# Revit family: IMH_ARR_1,9
name_source: partatom
category: Mechanical Equipment
units: mm (PartAtom-declared; Revit-internal decimal feet)

## family parameters
Always vertical = No
Cut with Voids When Loaded = No
Part Type = Normal
Room Calculation Point = No
Round Connector Dimension = Use Radius
Shared = No
Work Plane-Based = No

## types (44) — shared parameters
1.5 = 1.5 "
90 = 90.00°
BAD = No
BAD_CCW = No
BAD_CW = No
BAU = No
BAU_CCW = No
BAU_CW = No
BHD = No
BHD_CCW = No
BHD_CW = No
CCW = No
CW = Yes
DBD = No
DBD_CCW = No
DBD_CW = No
Four = 4 "
L_RAD = 18.156 "
Manufacturer = Loren Cook Company
NO = No
ONE EIGTH = 0.125 "
One_Inch = 1 "
TAD = No
TAD_CCW = No
TAD_CW = No
TAU = No
TAU_CCW = No
TAU_CW = No
THD = Yes
THD_CCW = No
THD_CW = Yes
Three = 3 "
Two_Feet = 24 "
Two_Inches = 2 "
UBD = No
UBD_CCW = No
UBD_CW = No
URL = www.lorencook.com
ZERO = 0.00°
zero-valued in all types: 0, FIRST_CURVE

## per-type parameters (varying)
- 70_MHA_ARR_1_9: 2S=8.5 "; 2T=2.375 "; 91_AA=8.019 "; A=6.625 "; A+.25=6.875 "; A/2=3.313 "; A/5=1.325 "; AA=8.813 "; B=5.875 "; B3=6.125 "; B4=-3.063 "; B5=3.063 "; BB=8.375 "; C=7 "; C3=3.375 "; C4=5.5 "; D=14.25 "; D3=-14.125 "; DimQ=7.438 "; E=9.688 "; E_LESS_2=7.688 "; F=21.063 "; G=26.25 "; H=24.188 "; HALF_B=2.938 "; HALF_C=3.5 "; HALF_E=4.844 "; HALF_M=4.156 "; HALF_P=0.281 "; HALF_T=0.594 "; J=4 "; K=9.188 "; L=9.688 "; M=8.313 "; M3=6.988 "; M4=6.988 "; Model=MHA; N=10.563 "; NA=3.938 "; NA3=1.969 "; NEG_D=-14.25 "; NEG_F=-21.063 "; P=0.563 "; R=14.875 "; R3=-11.156 "; R4=-11.156 "; S=4.25 "; SECOND_CURVE=0.828 "; T=1.188 "; T3=3.375 "; THIRD_CURVE=1.104 "; Type Comments=Industrial Material Handler Backward Inclined Flat Blade Belt Driven Single Width Single Inlet Arrangement 1_9; U=6.188 "; UNIT_SIZE=70; W=6 "; X=10.125 "; Y=9.25 "; Z=13.375 "
- 90_MHA_ARR_1_9: 2S=10.125 "; 2T=2.875 "; 91_AA=10.181 "; A=8.438 "; A+.25=8.688 "; A/2=4.219 "; A/5=1.688 "; AA=11.188 "; B=7.5 "; B3=7.75 "; B4=-3.875 "; B5=3.875 "; BB=10.625 "; C=9 "; C3=4.375 "; C4=6.5 "; D=15.25 "; D3=-15.125 "; DimQ=7.438 "; E=9.688 "; E_LESS_2=7.688 "; F=21.875 "; G=27.875 "; H=28.75 "; HALF_B=3.75 "; HALF_C=4.5 "; HALF_E=4.844 "; HALF_M=5.313 "; HALF_P=0.281 "; HALF_T=0.719 "; J=4 "; K=9.188 "; L=12.313 "; M=10.625 "; M3=8.938 "; M4=8.938 "; Model=MHA; N=13.5 "; NA=5.063 "; NA3=2.531 "; NEG_D=-15.25 "; NEG_F=-21.875 "; P=0.563 "; R=14.875 "; R3=-11.156 "; R4=-11.156 "; S=5.063 "; SECOND_CURVE=1.055 "; T=1.438 "; T3=3.875 "; THIRD_CURVE=1.406 "; Type Comments=Industrial Material Handler Backward Inclined Flat Blade Belt Driven Single Width Single Inlet Arrangement 1_9; U=7 "; UNIT_SIZE=90; W=6 "; X=12.938 "; Y=11.75 "; Z=17.063 "
- 110_MHA_ARR_1_9: 2S=13 "; 2T=2.875 "; 91_AA=12.513 "; A=10.375 "; A+.25=10.625 "; A/2=5.188 "; A/5=2.075 "; AA=13.75 "; B=9.125 "; B3=9.375 "; B4=-4.688 "; B5=4.688 "; BB=13.063 "; C=11 "; C3=5.375 "; C4=7.5 "; D=18.75 "; D3=-18.625 "; DimQ=8.25 "; E=9.688 "; E_LESS_2=7.688 "; F=25 "; G=32.875 "; H=35.188 "; HALF_B=4.563 "; HALF_C=5.5 "; HALF_E=4.844 "; HALF_M=6.5 "; HALF_P=0.281 "; HALF_T=0.719 "; J=4 "; K=9.188 "; L=15.063 "; M=13 "; M3=10.925 "; M4=10.925 "; Model=MHA; N=16.438 "; NA=6.063 "; NA3=3.031 "; NEG_D=-18.75 "; NEG_F=-25 "; P=0.563 "; R=16.5 "; R3=-12.375 "; R4=-12.375 "; S=6.5 "; SECOND_CURVE=1.297 "; T=1.438 "; T3=3.875 "; THIRD_CURVE=1.729 "; Type Comments=Industrial Material Handler Backward Inclined Flat Blade Belt Driven Single Width Single Inlet Arrangement 1_9; U=8.813 "; UNIT_SIZE=110; W=8 "; X=15.75 "; Y=14.438 "; Z=20.813 "
- 130_MHA_ARR_1_9: 2S=14.75 "; 2T=3.375 "; 91_AA=14.731 "; A=12.188 "; A+.25=12.438 "; A/2=6.094 "; A/5=2.438 "; AA=16.188 "; B=10.875 "; B3=11.125 "; B4=-5.563 "; B5=5.563 "; BB=15.375 "; C=13 "; C3=6.375 "; C4=8.5 "; D=21.75 "; D3=-21.625 "; DimQ=8.375 "; E=11.75 "; E_LESS_2=9.75 "; F=26.188 "; G=34.875 "; H=41.188 "; HALF_B=5.438 "; HALF_C=6.5 "; HALF_E=5.875 "; HALF_M=7.688 "; HALF_P=0.344 "; HALF_T=0.844 "; J=5 "; K=11 "; L=17.813 "; M=15.375 "; M3=12.938 "; M4=12.938 "; Model=MHA; N=19.438 "; NA=7.25 "; NA3=3.625 "; NEG_D=-21.75 "; NEG_F=-26.188 "; P=0.688 "; R=16.75 "; R3=-12.563 "; R4=-12.563 "; S=7.375 "; SECOND_CURVE=1.523 "; T=1.688 "; T3=4.375 "; THIRD_CURVE=2.031 "; Type Comments=Industrial Material Handler Backward Inclined Flat Blade Belt Driven Single Width Single Inlet Arrangement 1_9; U=9.813 "; UNIT_SIZE=130; W=8 "; X=18.625 "; Y=17 "; Z=24.625 "
- 150_MHA_ARR_1_9: 2S=16.438 "; 2T=3.875 "; 91_AA=17.176 "; A=14.063 "; A+.25=14.313 "; A/2=7.031 "; A/5=2.813 "; AA=18.875 "; B=12.563 "; B3=12.813 "; B4=-6.406 "; B5=6.406 "; BB=18 "; C=15 "; C3=7.375 "; C4=9.5 "; D=25.25 "; D3=-25.125 "; DimQ=10.75 "; E=13 "; E_LESS_2=11 "; F=31.75 "; G=41.313 "; H=47.625 "; HALF_B=6.281 "; HALF_C=7.5 "; HALF_E=6.5 "; HALF_M=8.875 "; HALF_P=0.344 "; HALF_T=0.969 "; J=5 "; K=12.25 "; L=20.625 "; M=17.75 "; M3=14.938 "; M4=14.938 "; Model=MHA; N=22.375 "; NA=8.313 "; NA3=4.156 "; NEG_D=-25.25 "; NEG_F=-31.75 "; P=0.688 "; R=21.5 "; R3=-16.125 "; R4=-16.125 "; S=8.219 "; SECOND_CURVE=1.758 "; T=1.938 "; T3=4.875 "; THIRD_CURVE=2.344 "; Type Comments=Industrial Material Handler Backward Inclined Flat Blade Belt Driven Single Width Single Inlet Arrangement 1_9; U=10.688 "; UNIT_SIZE=150; W=8 "; X=21.5 "; Y=19.75 "; Z=28.375 "
- 170_MHA_ARR_1_9: 2S=18.125 "; 2T=4.375 "; 91_AA=19.338 "; A=16 "; A+.25=16.25 "; A/2=8 "; A/5=3.2 "; AA=21.25 "; B=14.25 "; B3=14.5 "; B4=-7.25 "; B5=7.25 "; BB=20.25 "; C=17 "; C3=8.375 "; C4=10.5 "; D=28.25 "; D3=-28.125 "; DimQ=10.75 "; E=13.875 "; E_LESS_2=11.875 "; F=32.563 "; G=43 "; H=53.625 "; HALF_B=7.125 "; HALF_C=8.5 "; HALF_E=6.938 "; HALF_M=10.063 "; HALF_P=0.344 "; HALF_T=1.094 "; J=6 "; K=13.125 "; L=23.75 "; M=20.125 "; M3=16.925 "; M4=16.925 "; Model=MHA; N=25.375 "; NA=9.375 "; NA3=4.688 "; NEG_D=-28.25 "; NEG_F=-32.563 "; P=0.688 "; R=21.5 "; R3=-16.125 "; R4=-16.125 "; S=9.063 "; SECOND_CURVE=2 "; T=2.188 "; T3=5.375 "; THIRD_CURVE=2.667 "; Type Comments=Industrial Material Handler Backward Inclined Flat Blade Belt Driven Single Width Single Inlet Arrangement 1_9; U=11.5 "; UNIT_SIZE=170; W=8 "; X=24.563 "; Y=22.5 "; Z=32.188 "
- 190_MHA_ARR_1_9: 2S=19.875 "; 2T=4.875 "; 91_AA=21.613 "; A=17.813 "; A+.25=18.063 "; A/2=8.906 "; A/5=3.563 "; AA=23.75 "; B=15.875 "; B3=16.125 "; B4=-8.063 "; B5=8.063 "; BB=22.625 "; C=19 "; C3=9.375 "; C4=11.5 "; D=31.25 "; D3=-31.125 "; DimQ=11.375 "; E=15.313 "; E_LESS_2=13.313 "; F=34.688 "; G=46 "; H=59.5 "; HALF_B=7.938 "; HALF_C=9.5 "; HALF_E=7.656 "; HALF_M=11.219 "; HALF_P=0.344 "; HALF_T=1.219 "; J=6 "; K=14.563 "; L=25.938 "; M=22.438 "; M3=18.875 "; M4=18.875 "; Model=MHA; N=28.25 "; NA=10.438 "; NA3=5.219 "; NEG_D=-31.25 "; NEG_F=-34.688 "; P=0.688 "; R=22.75 "; R3=-17.063 "; R4=-17.063 "; S=9.938 "; SECOND_CURVE=2.227 "; T=2.438 "; T3=5.875 "; THIRD_CURVE=2.969 "; Type Comments=Industrial Material Handler Backward Inclined Flat Blade Belt Driven Single Width Single Inlet Arrangement 1_9; U=12.313 "; UNIT_SIZE=190; W=8 "; X=27.125 "; Y=24.875 "; Z=35.813 "
- 210_MHA_ARR_1_9: 2S=21.313 "; 2T=4.875 "; 91_AA=23.433 "; A=19.75 "; A+.25=20 "; A/2=9.875 "; A/5=3.95 "; AA=25.75 "; B=17.563 "; B3=17.813 "; B4=-8.906 "; B5=8.906 "; BB=24.375 "; C=21 "; C3=10.375 "; C4=12.5 "; D=34.5 "; D3=-34.375 "; DimQ=12.75 "; E=16.563 "; E_LESS_2=14.563 "; F=38.25 "; G=50.375 "; H=65.75 "; HALF_B=8.781 "; HALF_C=10.5 "; HALF_E=8.281 "; HALF_M=11.5 "; HALF_P=0.344 "; HALF_T=1.219 "; J=6 "; K=15.813 "; L=28.5 "; M=23 "; M3=19.05 "; M4=19.05 "; Model=MHA; N=31.25 "; NA=11.5 "; NA3=5.75 "; NEG_D=-34.5 "; NEG_F=-38.25 "; P=0.688 "; R=25.5 "; R3=-19.125 "; R4=-19.125 "; S=10.656 "; SECOND_CURVE=2.469 "; T=2.438 "; T3=5.875 "; THIRD_CURVE=3.292 "; Type Comments=Industrial Material Handler Backward Inclined Flat Blade Belt Driven Single Width Single Inlet Arrangement 1_9; U=13.188 "; UNIT_SIZE=210; W=8 "; X=29.875 "; Y=27.125 "; Z=38.375 "
- 230_MHA_ARR_1_9: 2S=24.625 "; 2T=5.375 "; 91_AA=25.764 "; A=21.625 "; A+.25=21.875 "; A/2=10.813 "; A/5=4.325 "; AA=28.313 "; B=19.25 "; B3=19.5 "; B4=-9.75 "; B5=9.75 "; BB=26.813 "; C=23 "; C3=11.375 "; C4=13.5 "; D=37.5 "; D3=-37.375 "; DimQ=13.438 "; E=18.813 "; E_LESS_2=16.813 "; F=41.125 "; G=55.25 "; H=71.813 "; HALF_B=9.625 "; HALF_C=11.5 "; HALF_E=9.406 "; HALF_M=13 "; HALF_P=0.406 "; HALF_T=1.344 "; J=7 "; K=17.563 "; L=31.25 "; M=26 "; M3=21.675 "; M4=21.675 "; Model=MHA; N=34.313 "; NA=12.688 "; NA3=6.344 "; NEG_D=-37.5 "; NEG_F=-41.125 "; P=0.813 "; R=26.875 "; R3=-20.156 "; R4=-20.156 "; S=12.313 "; SECOND_CURVE=2.703 "; T=2.688 "; T3=6.375 "; THIRD_CURVE=3.604 "; Type Comments=Industrial Material Handler Backward Inclined Flat Blade Belt Driven Single Width Single Inlet Arrangement 1_9; U=15.125 "; UNIT_SIZE=230; W=8 "; X=32.813 "; Y=29.813 "; Z=42.625 "
- 260_MHA_ARR_1_9: 2S=27.125 "; 2T=5.375 "; 91_AA=29.006 "; A=24.438 "; A+.25=24.688 "; A/2=12.219 "; A/5=4.888 "; AA=31.875 "; B=21.75 "; B3=22 "; B4=-11 "; B5=11 "; BB=30.25 "; C=26 "; C3=12.875 "; C4=15 "; D=41.75 "; D3=-41.625 "; DimQ=13.875 "; E=20.625 "; E_LESS_2=18.625 "; F=43.938 "; G=58.688 "; H=82.938 "; HALF_B=10.875 "; HALF_C=13 "; HALF_E=10.313 "; HALF_M=14.5 "; HALF_P=0.406 "; HALF_T=1.344 "; J=7 "; K=19.375 "; L=35.125 "; M=29 "; M3=24.113 "; M4=24.113 "; Model=MHA; N=41.188 "; NA=16.75 "; NA3=8.375 "; NEG_D=-41.75 "; NEG_F=-43.938 "; P=0.813 "; R=27.75 "; R3=-20.813 "; R4=-20.813 "; S=13.563 "; SECOND_CURVE=3.055 "; T=2.688 "; T3=6.375 "; THIRD_CURVE=4.073 "; Type Comments=Industrial Material Handler Backward Inclined Flat Blade Belt Driven Single Width Single Inlet Arrangement 1_9; U=16.375 "; UNIT_SIZE=260; W=8 "; X=38.188 "; Y=33.5 "; Z=49.625 "
- 290_MHA_ARR_1_9: 2S=29.625 "; 2T=5.875 "; 91_AA=32.533 "; A=27.313 "; A+.25=27.563 "; A/2=13.656 "; A/5=5.463 "; AA=35.75 "; B=24.25 "; B3=24.5 "; B4=-12.25 "; B5=12.25 "; BB=33.875 "; C=29 "; C3=14.375 "; C4=16.5 "; D=46.5 "; D3=-46.375 "; DimQ=14.375 "; E=22.5 "; E_LESS_2=20.5 "; F=45.563 "; G=62.188 "; H=92.5 "; HALF_B=12.125 "; HALF_C=14.5 "; HALF_E=11.25 "; HALF_M=15.875 "; HALF_P=0.406 "; HALF_T=1.469 "; J=8 "; K=21.25 "; L=39.5 "; M=31.75 "; M3=26.288 "; M4=26.288 "; Model=MHA; N=45.875 "; NA=18.563 "; NA3=9.281 "; NEG_D=-46.5 "; NEG_F=-45.563 "; P=0.813 "; R=28.75 "; R3=-21.563 "; R4=-21.563 "; S=14.813 "; SECOND_CURVE=3.414 "; T=2.938 "; T3=6.875 "; THIRD_CURVE=4.552 "; Type Comments=Industrial Material Handler Backward Inclined Flat Blade Belt Driven Single Width Single Inlet Arrangement 1_9; U=17.625 "; UNIT_SIZE=290; W=8 "; X=42.688 "; Y=37.625 "; Z=54.875 "
- 110_MHB_ARR_1_9: 2S=13 "; 2T=2.875 "; 91_AA=12.513 "; A=10.375 "; A+.25=10.625 "; A/2=5.188 "; A/5=2.075 "; AA=13.75 "; B=9.125 "; B3=9.375 "; B4=-4.688 "; B5=4.688 "; BB=13.063 "; C=11 "; C3=5.375 "; C4=7.5 "; D=18.75 "; D3=-18.625 "; DimQ=8.25 "; E=9.688 "; E_LESS_2=7.688 "; F=25 "; G=32.875 "; H=35.188 "; HALF_B=4.563 "; HALF_C=5.5 "; HALF_E=4.844 "; HALF_M=6.5 "; HALF_P=0.281 "; HALF_T=0.719 "; J=4 "; K=9.188 "; L=15.063 "; M=13 "; M3=10.925 "; M4=10.925 "; Model=MHB; N=16.438 "; NA=6.063 "; NA3=3.031 "; NEG_D=-18.75 "; NEG_F=-25 "; P=0.563 "; R=16.5 "; R3=-12.375 "; R4=-12.375 "; S=6.5 "; SECOND_CURVE=1.297 "; T=1.438 "; T3=3.875 "; THIRD_CURVE=1.729 "; Type Comments=Industrial Material Handler Backward Inclined Backplated Radial Blade Belt Driven Single Width Single Inlet Arrangement 1_9; U=8.813 "; UNIT_SIZE=110; W=8 "; X=15.75 "; Y=14.438 "; Z=20.813 "
- 110_MHR_ARR_1_9: 2S=13 "; 2T=2.875 "; 91_AA=12.513 "; A=10.375 "; A+.25=10.625 "; A/2=5.188 "; A/5=2.075 "; AA=13.75 "; B=9.125 "; B3=9.375 "; B4=-4.688 "; B5=4.688 "; BB=13.063 "; C=11 "; C3=5.375 "; C4=7.5 "; D=18.75 "; D3=-18.625 "; DimQ=8.25 "; E=9.688 "; E_LESS_2=7.688 "; F=25 "; G=32.875 "; H=35.188 "; HALF_B=4.563 "; HALF_C=5.5 "; HALF_E=4.844 "; HALF_M=6.5 "; HALF_P=0.281 "; HALF_T=0.719 "; J=4 "; K=9.188 "; L=15.063 "; M=13 "; M3=10.925 "; M4=10.925 "; Model=MHR; N=16.438 "; NA=6.063 "; NA3=3.031 "; NEG_D=-18.75 "; NEG_F=-25 "; P=0.563 "; R=16.5 "; R3=-12.375 "; R4=-12.375 "; S=6.5 "; SECOND_CURVE=1.297 "; T=1.438 "; T3=3.875 "; THIRD_CURVE=1.729 "; Type Comments=Industrial Material Handler Backward Inclined Reinforced Radial Blade Belt Driven Single Width Single Inlet Arrangement 1_9; U=8.813 "; UNIT_SIZE=110; W=8 "; X=15.75 "; Y=14.438 "; Z=20.813 "
- 130_MHB_ARR_1_9: 2S=14.75 "; 2T=3.375 "; 91_AA=14.731 "; A=12.188 "; A+.25=12.438 "; A/2=6.094 "; A/5=2.438 "; AA=16.188 "; B=10.875 "; B3=11.125 "; B4=-5.563 "; B5=5.563 "; BB=15.375 "; C=13 "; C3=6.375 "; C4=8.5 "; D=21.75 "; D3=-21.625 "; DimQ=8.375 "; E=11.75 "; E_LESS_2=9.75 "; F=26.188 "; G=34.875 "; H=41.188 "; HALF_B=5.438 "; HALF_C=6.5 "; HALF_E=5.875 "; HALF_M=7.688 "; HALF_P=0.344 "; HALF_T=0.844 "; J=5 "; K=11 "; L=17.813 "; M=15.375 "; M3=12.938 "; M4=12.938 "; Model=MHB; N=19.438 "; NA=7.25 "; NA3=3.625 "; NEG_D=-21.75 "; NEG_F=-26.188 "; P=0.688 "; R=16.75 "; R3=-12.563 "; R4=-12.563 "; S=7.375 "; SECOND_CURVE=1.523 "; T=1.688 "; T3=4.375 "; THIRD_CURVE=2.031 "; Type Comments=Industrial Material Handler Backward Inclined Backplated Radial Blade Belt Driven Single Width Single Inlet Arrangement 1_9; U=9.813 "; UNIT_SIZE=130; W=8 "; X=18.625 "; Y=17 "; Z=24.625 "
- 130_MHR_ARR_1_9: 2S=14.75 "; 2T=3.375 "; 91_AA=14.731 "; A=12.188 "; A+.25=12.438 "; A/2=6.094 "; A/5=2.438 "; AA=16.188 "; B=10.875 "; B3=11.125 "; B4=-5.563 "; B5=5.563 "; BB=15.375 "; C=13 "; C3=6.375 "; C4=8.5 "; D=21.75 "; D3=-21.625 "; DimQ=8.375 "; E=11.75 "; E_LESS_2=9.75 "; F=26.188 "; G=34.875 "; H=41.188 "; HALF_B=5.438 "; HALF_C=6.5 "; HALF_E=5.875 "; HALF_M=7.688 "; HALF_P=0.344 "; HALF_T=0.844 "; J=5 "; K=11 "; L=17.813 "; M=15.375 "; M3=12.938 "; M4=12.938 "; Model=MHR; N=19.438 "; NA=7.25 "; NA3=3.625 "; NEG_D=-21.75 "; NEG_F=-26.188 "; P=0.688 "; R=16.75 "; R3=-12.563 "; R4=-12.563 "; S=7.375 "; SECOND_CURVE=1.523 "; T=1.688 "; T3=4.375 "; THIRD_CURVE=2.031 "; Type Comments=Industrial Material Handler Backward Inclined Reinforced Radial Blade Belt Driven Single Width Single Inlet Arrangement 1_9; U=9.813 "; UNIT_SIZE=130; W=8 "; X=18.625 "; Y=17 "; Z=24.625 "
- 150_MHB_ARR_1_9: 2S=16.438 "; 2T=3.875 "; 91_AA=17.176 "; A=14.063 "; A+.25=14.313 "; A/2=7.031 "; A/5=2.813 "; AA=18.875 "; B=12.563 "; B3=12.813 "; B4=-6.406 "; B5=6.406 "; BB=18 "; C=15 "; C3=7.375 "; C4=9.5 "; D=25.25 "; D3=-25.125 "; DimQ=10.75 "; E=13 "; E_LESS_2=11 "; F=31.75 "; G=41.313 "; H=47.625 "; HALF_B=6.281 "; HALF_C=7.5 "; HALF_E=6.5 "; HALF_M=8.875 "; HALF_P=0.344 "; HALF_T=0.969 "; J=5 "; K=12.25 "; L=20.625 "; M=17.75 "; M3=14.938 "; M4=14.938 "; Model=MHB; N=22.375 "; NA=8.313 "; NA3=4.156 "; NEG_D=-25.25 "; NEG_F=-31.75 "; P=0.688 "; R=21.5 "; R3=-16.125 "; R4=-16.125 "; S=8.219 "; SECOND_CURVE=1.758 "; T=1.938 "; T3=4.875 "; THIRD_CURVE=2.344 "; Type Comments=Industrial Material Handler Backward Inclined Backplated Radial Blade Belt Driven Single Width Single Inlet Arrangement 1_9; U=10.688 "; UNIT_SIZE=150; W=8 "; X=21.5 "; Y=19.75 "; Z=28.375 "
- 150_MHR_ARR_1_9: 2S=16.438 "; 2T=3.875 "; 91_AA=17.176 "; A=14.063 "; A+.25=14.313 "; A/2=7.031 "; A/5=2.813 "; AA=18.875 "; B=12.563 "; B3=12.813 "; B4=-6.406 "; B5=6.406 "; BB=18 "; C=15 "; C3=7.375 "; C4=9.5 "; D=25.25 "; D3=-25.125 "; DimQ=10.75 "; E=13 "; E_LESS_2=11 "; F=31.75 "; G=41.313 "; H=47.625 "; HALF_B=6.281 "; HALF_C=7.5 "; HALF_E=6.5 "; HALF_M=8.875 "; HALF_P=0.344 "; HALF_T=0.969 "; J=5 "; K=12.25 "; L=20.625 "; M=17.75 "; M3=14.938 "; M4=14.938 "; Model=MHR; N=22.375 "; NA=8.313 "; NA3=4.156 "; NEG_D=-25.25 "; NEG_F=-31.75 "; P=0.688 "; R=21.5 "; R3=-16.125 "; R4=-16.125 "; S=8.219 "; SECOND_CURVE=1.758 "; T=1.938 "; T3=4.875 "; THIRD_CURVE=2.344 "; Type Comments=Industrial Material Handler Backward Inclined Reinforced Radial Blade Belt Driven Single Width Single Inlet Arrangement 1_9; U=10.688 "; UNIT_SIZE=150; W=8 "; X=21.5 "; Y=19.75 "; Z=28.375 "
- 170_MHB_ARR_1_9: 2S=18.125 "; 2T=4.375 "; 91_AA=19.338 "; A=16 "; A+.25=16.25 "; A/2=8 "; A/5=3.2 "; AA=21.25 "; B=14.25 "; B3=14.5 "; B4=-7.25 "; B5=7.25 "; BB=20.25 "; C=17 "; C3=8.375 "; C4=10.5 "; D=28.25 "; D3=-28.125 "; DimQ=10.75 "; E=13.875 "; E_LESS_2=11.875 "; F=32.563 "; G=43 "; H=53.625 "; HALF_B=7.125 "; HALF_C=8.5 "; HALF_E=6.938 "; HALF_M=10.063 "; HALF_P=0.344 "; HALF_T=1.094 "; J=6 "; K=13.125 "; L=23.75 "; M=20.125 "; M3=16.925 "; M4=16.925 "; Model=MHB; N=25.375 "; NA=9.375 "; NA3=4.688 "; NEG_D=-28.25 "; NEG_F=-32.563 "; P=0.688 "; R=21.5 "; R3=-16.125 "; R4=-16.125 "; S=9.063 "; SECOND_CURVE=2 "; T=2.188 "; T3=5.375 "; THIRD_CURVE=2.667 "; Type Comments=Industrial Material Handler Backward Inclined Backplated Radial Blade Belt Driven Single Width Single Inlet Arrangement 1_9; U=11.5 "; UNIT_SIZE=170; W=8 "; X=24.563 "; Y=22.5 "; Z=32.188 "
- 170_MHR_ARR_1_9: 2S=18.125 "; 2T=4.375 "; 91_AA=19.338 "; A=16 "; A+.25=16.25 "; A/2=8 "; A/5=3.2 "; AA=21.25 "; B=14.25 "; B3=14.5 "; B4=-7.25 "; B5=7.25 "; BB=20.25 "; C=17 "; C3=8.375 "; C4=10.5 "; D=28.25 "; D3=-28.125 "; DimQ=10.75 "; E=13.875 "; E_LESS_2=11.875 "; F=32.563 "; G=43 "; H=53.625 "; HALF_B=7.125 "; HALF_C=8.5 "; HALF_E=6.938 "; HALF_M=10.063 "; HALF_P=0.344 "; HALF_T=1.094 "; J=6 "; K=13.125 "; L=23.75 "; M=20.125 "; M3=16.925 "; M4=16.925 "; Model=MHR; N=25.375 "; NA=9.375 "; NA3=4.688 "; NEG_D=-28.25 "; NEG_F=-32.563 "; P=0.688 "; R=21.5 "; R3=-16.125 "; R4=-16.125 "; S=9.063 "; SECOND_CURVE=2 "; T=2.188 "; T3=5.375 "; THIRD_CURVE=2.667 "; Type Comments=Industrial Material Handler Backward Inclined Reinforced Radial Blade Belt Driven Single Width Single Inlet Arrangement 1_9; U=11.5 "; UNIT_SIZE=170; W=8 "; X=24.563 "; Y=22.5 "; Z=32.188 "
- 190_MHB_ARR_1_9: 2S=19.875 "; 2T=4.875 "; 91_AA=21.613 "; A=17.813 "; A+.25=18.063 "; A/2=8.906 "; A/5=3.563 "; AA=23.75 "; B=15.875 "; B3=16.125 "; B4=-8.063 "; B5=8.063 "; BB=22.625 "; C=19 "; C3=9.375 "; C4=11.5 "; D=31.25 "; D3=-31.125 "; DimQ=11.375 "; E=15.313 "; E_LESS_2=13.313 "; F=34.688 "; G=46 "; H=59.5 "; HALF_B=7.938 "; HALF_C=9.5 "; HALF_E=7.656 "; HALF_M=11.219 "; HALF_P=0.344 "; HALF_T=1.219 "; J=6 "; K=14.563 "; L=25.938 "; M=22.438 "; M3=18.875 "; M4=18.875 "; Model=MHB; N=28.25 "; NA=10.438 "; NA3=5.219 "; NEG_D=-31.25 "; NEG_F=-34.688 "; P=0.688 "; R=22.75 "; R3=-17.063 "; R4=-17.063 "; S=9.938 "; SECOND_CURVE=2.227 "; T=2.438 "; T3=5.875 "; THIRD_CURVE=2.969 "; Type Comments=Industrial Material Handler Backward Inclined Backplated Radial Blade Belt Driven Single Width Single Inlet Arrangement 1_9; U=12.313 "; UNIT_SIZE=190; W=8 "; X=27.125 "; Y=24.875 "; Z=35.813 "
- 190_MHR_ARR_1_9: 2S=19.875 "; 2T=4.875 "; 91_AA=21.613 "; A=17.813 "; A+.25=18.063 "; A/2=8.906 "; A/5=3.563 "; AA=23.75 "; B=15.875 "; B3=16.125 "; B4=-8.063 "; B5=8.063 "; BB=22.625 "; C=19 "; C3=9.375 "; C4=11.5 "; D=31.25 "; D3=-31.125 "; DimQ=11.375 "; E=15.313 "; E_LESS_2=13.313 "; F=34.688 "; G=46 "; H=59.5 "; HALF_B=7.938 "; HALF_C=9.5 "; HALF_E=7.656 "; HALF_M=11.219 "; HALF_P=0.344 "; HALF_T=1.219 "; J=6 "; K=14.563 "; L=25.938 "; M=22.438 "; M3=18.875 "; M4=18.875 "; Model=MHR; N=28.25 "; NA=10.438 "; NA3=5.219 "; NEG_D=-31.25 "; NEG_F=-34.688 "; P=0.688 "; R=22.75 "; R3=-17.063 "; R4=-17.063 "; S=9.938 "; SECOND_CURVE=2.227 "; T=2.438 "; T3=5.875 "; THIRD_CURVE=2.969 "; Type Comments=Industrial Material Handler Backward Inclined Reinforced Radial Blade Belt Driven Single Width Single Inlet Arrangement 1_9; U=12.313 "; UNIT_SIZE=190; W=8 "; X=27.125 "; Y=24.875 "; Z=35.813 "
- 210_MHB_ARR_1_9: 2S=21.313 "; 2T=4.875 "; 91_AA=23.433 "; A=19.75 "; A+.25=20 "; A/2=9.875 "; A/5=3.95 "; AA=25.75 "; B=17.563 "; B3=17.813 "; B4=-8.906 "; B5=8.906 "; BB=24.375 "; C=21 "; C3=10.375 "; C4=12.5 "; D=34.5 "; D3=-34.375 "; DimQ=12.75 "; E=16.563 "; E_LESS_2=14.563 "; F=38.25 "; G=50.375 "; H=65.75 "; HALF_B=8.781 "; HALF_C=10.5 "; HALF_E=8.281 "; HALF_M=11.5 "; HALF_P=0.344 "; HALF_T=1.219 "; J=6 "; K=15.813 "; L=28.5 "; M=23 "; M3=19.05 "; M4=19.05 "; Model=MHB; N=31.25 "; NA=11.5 "; NA3=5.75 "; NEG_D=-34.5 "; NEG_F=-38.25 "; P=0.688 "; R=25.5 "; R3=-19.125 "; R4=-19.125 "; S=10.656 "; SECOND_CURVE=2.469 "; T=2.438 "; T3=5.875 "; THIRD_CURVE=3.292 "; Type Comments=Industrial Material Handler Backward Inclined Backplated Radial Blade Belt Driven Single Width Single Inlet Arrangement 1_9; U=13.188 "; UNIT_SIZE=210; W=8 "; X=29.875 "; Y=27.125 "; Z=38.375 "
- 210_MHR_ARR_1_9: 2S=21.313 "; 2T=4.875 "; 91_AA=23.433 "; A=19.75 "; A+.25=20 "; A/2=9.875 "; A/5=3.95 "; AA=25.75 "; B=17.563 "; B3=17.813 "; B4=-8.906 "; B5=8.906 "; BB=24.375 "; C=21 "; C3=10.375 "; C4=12.5 "; D=34.5 "; D3=-34.375 "; DimQ=12.75 "; E=16.563 "; E_LESS_2=14.563 "; F=38.25 "; G=50.375 "; H=65.75 "; HALF_B=8.781 "; HALF_C=10.5 "; HALF_E=8.281 "; HALF_M=11.5 "; HALF_P=0.344 "; HALF_T=1.219 "; J=6 "; K=15.813 "; L=28.5 "; M=23 "; M3=19.05 "; M4=19.05 "; Model=MHR; N=31.25 "; NA=11.5 "; NA3=5.75 "; NEG_D=-34.5 "; NEG_F=-38.25 "; P=0.688 "; R=25.5 "; R3=-19.125 "; R4=-19.125 "; S=10.656 "; SECOND_CURVE=2.469 "; T=2.438 "; T3=5.875 "; THIRD_CURVE=3.292 "; Type Comments=Industrial Material Handler Backward Inclined Reinforced Radial Blade Belt Driven Single Width Single Inlet Arrangement 1_9; U=13.188 "; UNIT_SIZE=210; W=8 "; X=29.875 "; Y=27.125 "; Z=38.375 "
- 230_MHB_ARR_1_9: 2S=24.625 "; 2T=5.375 "; 91_AA=25.764 "; A=21.625 "; A+.25=21.875 "; A/2=10.813 "; A/5=4.325 "; AA=28.313 "; B=19.25 "; B3=19.5 "; B4=-9.75 "; B5=9.75 "; BB=26.813 "; C=23 "; C3=11.375 "; C4=13.5 "; D=37.5 "; D3=-37.375 "; DimQ=13.438 "; E=18.813 "; E_LESS_2=16.813 "; F=41.125 "; G=55.25 "; H=71.813 "; HALF_B=9.625 "; HALF_C=11.5 "; HALF_E=9.406 "; HALF_M=13 "; HALF_P=0.406 "; HALF_T=1.344 "; J=7 "; K=17.563 "; L=31.25 "; M=26 "; M3=21.675 "; M4=21.675 "; Model=MHB; N=34.313 "; NA=12.688 "; NA3=6.344 "; NEG_D=-37.5 "; NEG_F=-41.125 "; P=0.813 "; R=26.875 "; R3=-20.156 "; R4=-20.156 "; S=12.313 "; SECOND_CURVE=2.703 "; T=2.688 "; T3=6.375 "; THIRD_CURVE=3.604 "; Type Comments=Industrial Material Handler Backward Inclined Backplated Radial Blade Belt Driven Single Width Single Inlet Arrangement 1_9; U=15.125 "; UNIT_SIZE=230; W=8 "; X=32.813 "; Y=29.813 "; Z=42.625 "
- 230_MHR_ARR_1_9: 2S=24.625 "; 2T=5.375 "; 91_AA=25.764 "; A=21.625 "; A+.25=21.875 "; A/2=10.813 "; A/5=4.325 "; AA=28.313 "; B=19.25 "; B3=19.5 "; B4=-9.75 "; B5=9.75 "; BB=26.813 "; C=23 "; C3=11.375 "; C4=13.5 "; D=37.5 "; D3=-37.375 "; DimQ=13.438 "; E=18.813 "; E_LESS_2=16.813 "; F=41.125 "; G=55.25 "; H=71.813 "; HALF_B=9.625 "; HALF_C=11.5 "; HALF_E=9.406 "; HALF_M=13 "; HALF_P=0.406 "; HALF_T=1.344 "; J=7 "; K=17.563 "; L=31.25 "; M=26 "; M3=21.675 "; M4=21.675 "; Model=MHR; N=34.313 "; NA=12.688 "; NA3=6.344 "; NEG_D=-37.5 "; NEG_F=-41.125 "; P=0.813 "; R=26.875 "; R3=-20.156 "; R4=-20.156 "; S=12.313 "; SECOND_CURVE=2.703 "; T=2.688 "; T3=6.375 "; THIRD_CURVE=3.604 "; Type Comments=Industrial Material Handler Backward Inclined Reinforced Radial Blade Belt Driven Single Width Single Inlet Arrangement 1_9; U=15.125 "; UNIT_SIZE=230; W=8 "; X=32.813 "; Y=29.813 "; Z=42.625 "
- 260_MHB_ARR_1_9: 2S=27.125 "; 2T=5.375 "; 91_AA=29.006 "; A=24.438 "; A+.25=24.688 "; A/2=12.219 "; A/5=4.888 "; AA=31.875 "; B=21.75 "; B3=22 "; B4=-11 "; B5=11 "; BB=30.25 "; C=26 "; C3=12.875 "; C4=15 "; D=41.75 "; D3=-41.625 "; DimQ=13.875 "; E=20.625 "; E_LESS_2=18.625 "; F=43.938 "; G=58.688 "; H=82.938 "; HALF_B=10.875 "; HALF_C=13 "; HALF_E=10.313 "; HALF_M=14.5 "; HALF_P=0.406 "; HALF_T=1.344 "; J=7 "; K=19.375 "; L=35.125 "; M=29 "; M3=24.113 "; M4=24.113 "; Model=MHB; N=41.188 "; NA=16.75 "; NA3=8.375 "; NEG_D=-41.75 "; NEG_F=-43.938 "; P=0.813 "; R=27.75 "; R3=-20.813 "; R4=-20.813 "; S=13.563 "; SECOND_CURVE=3.055 "; T=2.688 "; T3=6.375 "; THIRD_CURVE=4.073 "; Type Comments=Industrial Material Handler Backward Inclined Backplated Radial Blade Belt Driven Single Width Single Inlet Arrangement 1_9; U=16.375 "; UNIT_SIZE=260; W=8 "; X=38.188 "; Y=33.5 "; Z=49.625 "
- 260_MHR_ARR_1_9: 2S=27.125 "; 2T=5.375 "; 91_AA=29.006 "; A=24.438 "; A+.25=24.688 "; A/2=12.219 "; A/5=4.888 "; AA=31.875 "; B=21.75 "; B3=22 "; B4=-11 "; B5=11 "; BB=30.25 "; C=26 "; C3=12.875 "; C4=15 "; D=41.75 "; D3=-41.625 "; DimQ=13.875 "; E=20.625 "; E_LESS_2=18.625 "; F=43.938 "; G=58.688 "; H=82.938 "; HALF_B=10.875 "; HALF_C=13 "; HALF_E=10.313 "; HALF_M=14.5 "; HALF_P=0.406 "; HALF_T=1.344 "; J=7 "; K=19.375 "; L=35.125 "; M=29 "; M3=24.113 "; M4=24.113 "; Model=MHR; N=41.188 "; NA=16.75 "; NA3=8.375 "; NEG_D=-41.75 "; NEG_F=-43.938 "; P=0.813 "; R=27.75 "; R3=-20.813 "; R4=-20.813 "; S=13.563 "; SECOND_CURVE=3.055 "; T=2.688 "; T3=6.375 "; THIRD_CURVE=4.073 "; Type Comments=Industrial Material Handler Backward Inclined Reinforced Radial Blade Belt Driven Single Width Single Inlet Arrangement 1_9; U=16.375 "; UNIT_SIZE=260; W=8 "; X=38.188 "; Y=33.5 "; Z=49.625 "
- 290_MHB_ARR_1_9: 2S=29.625 "; 2T=5.875 "; 91_AA=32.533 "; A=27.313 "; A+.25=27.563 "; A/2=13.656 "; A/5=5.463 "; AA=35.75 "; B=24.25 "; B3=24.5 "; B4=-12.25 "; B5=12.25 "; BB=33.875 "; C=29 "; C3=14.375 "; C4=16.5 "; D=46.5 "; D3=-46.375 "; DimQ=14.375 "; E=22.5 "; E_LESS_2=20.5 "; F=45.563 "; G=62.188 "; H=92.5 "; HALF_B=12.125 "; HALF_C=14.5 "; HALF_E=11.25 "; HALF_M=15.875 "; HALF_P=0.406 "; HALF_T=1.469 "; J=8 "; K=21.25 "; L=39.5 "; M=31.75 "; M3=26.288 "; M4=26.288 "; Model=MHB; N=45.875 "; NA=18.563 "; NA3=9.281 "; NEG_D=-46.5 "; NEG_F=-45.563 "; P=0.813 "; R=28.75 "; R3=-21.563 "; R4=-21.563 "; S=14.813 "; SECOND_CURVE=3.414 "; T=2.938 "; T3=6.875 "; THIRD_CURVE=4.552 "; Type Comments=Industrial Material Handler Backward Inclined Backplated Radial Blade Belt Driven Single Width Single Inlet Arrangement 1_9; U=17.625 "; UNIT_SIZE=290; W=8 "; X=42.688 "; Y=37.625 "; Z=54.875 "
- 290_MHR_ARR_1_9: 2S=29.625 "; 2T=5.875 "; 91_AA=32.533 "; A=27.313 "; A+.25=27.563 "; A/2=13.656 "; A/5=5.463 "; AA=35.75 "; B=24.25 "; B3=24.5 "; B4=-12.25 "; B5=12.25 "; BB=33.875 "; C=29 "; C3=14.375 "; C4=16.5 "; D=46.5 "; D3=-46.375 "; DimQ=14.375 "; E=22.5 "; E_LESS_2=20.5 "; F=45.563 "; G=62.188 "; H=92.5 "; HALF_B=12.125 "; HALF_C=14.5 "; HALF_E=11.25 "; HALF_M=15.875 "; HALF_P=0.406 "; HALF_T=1.469 "; J=8 "; K=21.25 "; L=39.5 "; M=31.75 "; M3=26.288 "; M4=26.288 "; Model=MHR; N=45.875 "; NA=18.563 "; NA3=9.281 "; NEG_D=-46.5 "; NEG_F=-45.563 "; P=0.813 "; R=28.75 "; R3=-21.563 "; R4=-21.563 "; S=14.813 "; SECOND_CURVE=3.414 "; T=2.938 "; T3=6.875 "; THIRD_CURVE=4.552 "; Type Comments=Industrial Material Handler Backward Inclined Reinforced Radial Blade Belt Driven Single Width Single Inlet Arrangement 1_9; U=17.625 "; UNIT_SIZE=290; W=8 "; X=42.688 "; Y=37.625 "; Z=54.875 "
- 70_MHB_ARR_1_9: 2S=8.5 "; 2T=2.375 "; 91_AA=8.019 "; A=6.625 "; A+.25=6.875 "; A/2=3.313 "; A/5=1.325 "; AA=8.813 "; B=5.875 "; B3=6.125 "; B4=-3.063 "; B5=3.063 "; BB=8.375 "; C=7 "; C3=3.375 "; C4=5.5 "; D=14.25 "; D3=-14.125 "; DimQ=7.438 "; E=9.688 "; E_LESS_2=7.688 "; F=21.063 "; G=26.25 "; H=24.188 "; HALF_B=2.938 "; HALF_C=3.5 "; HALF_E=4.844 "; HALF_M=4.156 "; HALF_P=0.281 "; HALF_T=0.594 "; J=4 "; K=9.188 "; L=9.688 "; M=8.313 "; M3=6.988 "; M4=6.988 "; Model=MHB; N=10.563 "; NA=3.938 "; NA3=1.969 "; NEG_D=-14.25 "; NEG_F=-21.063 "; P=0.563 "; R=14.875 "; R3=-11.156 "; R4=-11.156 "; S=4.25 "; SECOND_CURVE=0.828 "; T=1.188 "; T3=3.375 "; THIRD_CURVE=1.104 "; Type Comments=Industrial Material Handler Backward Inclined Backplated Radial Blade Belt Driven Single Width Single Inlet Arrangement 1_9; U=6.188 "; UNIT_SIZE=70; W=6 "; X=10.125 "; Y=9.25 "; Z=13.375 "
- 70_MHR_ARR_1_9: 2S=8.5 "; 2T=2.375 "; 91_AA=8.019 "; A=6.625 "; A+.25=6.875 "; A/2=3.313 "; A/5=1.325 "; AA=8.813 "; B=5.875 "; B3=6.125 "; B4=-3.063 "; B5=3.063 "; BB=8.375 "; C=7 "; C3=3.375 "; C4=5.5 "; D=14.25 "; D3=-14.125 "; DimQ=7.438 "; E=9.688 "; E_LESS_2=7.688 "; F=21.063 "; G=26.25 "; H=24.188 "; HALF_B=2.938 "; HALF_C=3.5 "; HALF_E=4.844 "; HALF_M=4.156 "; HALF_P=0.281 "; HALF_T=0.594 "; J=4 "; K=9.188 "; L=9.688 "; M=8.313 "; M3=6.988 "; M4=6.988 "; Model=MHR; N=10.563 "; NA=3.938 "; NA3=1.969 "; NEG_D=-14.25 "; NEG_F=-21.063 "; P=0.563 "; R=14.875 "; R3=-11.156 "; R4=-11.156 "; S=4.25 "; SECOND_CURVE=0.828 "; T=1.188 "; T3=3.375 "; THIRD_CURVE=1.104 "; Type Comments=Industrial Material Handler Backward Inclined Reinforced Radial Blade Belt Driven Single Width Single Inlet Arrangement 1_9; U=6.188 "; UNIT_SIZE=70; W=6 "; X=10.125 "; Y=9.25 "; Z=13.375 "
- 90_MHB_ARR_1_9: 2S=10.125 "; 2T=2.875 "; 91_AA=10.181 "; A=8.438 "; A+.25=8.688 "; A/2=4.219 "; A/5=1.688 "; AA=11.188 "; B=7.5 "; B3=7.75 "; B4=-3.875 "; B5=3.875 "; BB=10.625 "; C=9 "; C3=4.375 "; C4=6.5 "; D=15.25 "; D3=-15.125 "; DimQ=7.438 "; E=9.688 "; E_LESS_2=7.688 "; F=21.875 "; G=27.875 "; H=28.75 "; HALF_B=3.75 "; HALF_C=4.5 "; HALF_E=4.844 "; HALF_M=5.313 "; HALF_P=0.281 "; HALF_T=0.719 "; J=4 "; K=9.188 "; L=12.313 "; M=10.625 "; M3=8.938 "; M4=8.938 "; Model=MHB; N=13.5 "; NA=5.063 "; NA3=2.531 "; NEG_D=-15.25 "; NEG_F=-21.875 "; P=0.563 "; R=14.875 "; R3=-11.156 "; R4=-11.156 "; S=5.063 "; SECOND_CURVE=1.055 "; T=1.438 "; T3=3.875 "; THIRD_CURVE=1.406 "; Type Comments=Industrial Material Handler Backward Inclined Backplated Radial Blade Belt Driven Single Width Single Inlet Arrangement 1_9; U=7 "; UNIT_SIZE=90; W=6 "; X=12.938 "; Y=11.75 "; Z=17.063 "
- 90_MHR_ARR_1_9: 2S=10.125 "; 2T=2.875 "; 91_AA=10.181 "; A=8.438 "; A+.25=8.688 "; A/2=4.219 "; A/5=1.688 "; AA=11.188 "; B=7.5 "; B3=7.75 "; B4=-3.875 "; B5=3.875 "; BB=10.625 "; C=9 "; C3=4.375 "; C4=6.5 "; D=15.25 "; D3=-15.125 "; DimQ=7.438 "; E=9.688 "; E_LESS_2=7.688 "; F=21.875 "; G=27.875 "; H=28.75 "; HALF_B=3.75 "; HALF_C=4.5 "; HALF_E=4.844 "; HALF_M=5.313 "; HALF_P=0.281 "; HALF_T=0.719 "; J=4 "; K=9.188 "; L=12.313 "; M=10.625 "; M3=8.938 "; M4=8.938 "; Model=MHR; N=13.5 "; NA=5.063 "; NA3=2.531 "; NEG_D=-15.25 "; NEG_F=-21.875 "; P=0.563 "; R=14.875 "; R3=-11.156 "; R4=-11.156 "; S=5.063 "; SECOND_CURVE=1.055 "; T=1.438 "; T3=3.875 "; THIRD_CURVE=1.406 "; Type Comments=Industrial Material Handler Backward Inclined Reinforced Radial Blade Belt Driven Single Width Single Inlet Arrangement 1_9; U=7 "; UNIT_SIZE=90; W=6 "; X=12.938 "; Y=11.75 "; Z=17.063 "
- 110_MH_ARR_1_9: 2S=13 "; 2T=2.875 "; 91_AA=12.513 "; A=10.375 "; A+.25=10.625 "; A/2=5.188 "; A/5=2.075 "; AA=13.75 "; B=9.125 "; B3=9.375 "; B4=-4.688 "; B5=4.688 "; BB=13.063 "; C=11 "; C3=5.375 "; C4=7.5 "; D=18.75 "; D3=-18.625 "; DimQ=8.25 "; E=9.688 "; E_LESS_2=7.688 "; F=25 "; G=32.875 "; H=35.188 "; HALF_B=4.563 "; HALF_C=5.5 "; HALF_E=4.844 "; HALF_M=6.5 "; HALF_P=0.281 "; HALF_T=0.719 "; J=4 "; K=9.188 "; L=15.063 "; M=13 "; M3=10.925 "; M4=10.925 "; Model=MH; N=16.438 "; NA=6.063 "; NA3=3.031 "; NEG_D=-18.75 "; NEG_F=-25 "; P=0.563 "; R=16.5 "; R3=-12.375 "; R4=-12.375 "; S=6.5 "; SECOND_CURVE=1.297 "; T=1.438 "; T3=3.875 "; THIRD_CURVE=1.729 "; Type Comments=Industrial Material Handler Backward Inclined Radial Blade Belt Driven Single Width Single Inlet Arrangement 1_9; U=8.813 "; UNIT_SIZE=110; W=8 "; X=15.75 "; Y=14.438 "; Z=20.813 "
- 130_MH_ARR_1_9: 2S=14.75 "; 2T=3.375 "; 91_AA=14.731 "; A=12.188 "; A+.25=12.438 "; A/2=6.094 "; A/5=2.438 "; AA=16.188 "; B=10.875 "; B3=11.125 "; B4=-5.563 "; B5=5.563 "; BB=15.375 "; C=13 "; C3=6.375 "; C4=8.5 "; D=21.75 "; D3=-21.625 "; DimQ=8.375 "; E=11.75 "; E_LESS_2=9.75 "; F=26.188 "; G=34.875 "; H=41.188 "; HALF_B=5.438 "; HALF_C=6.5 "; HALF_E=5.875 "; HALF_M=7.688 "; HALF_P=0.344 "; HALF_T=0.844 "; J=5 "; K=11 "; L=17.813 "; M=15.375 "; M3=12.938 "; M4=12.938 "; Model=MH; N=19.438 "; NA=7.25 "; NA3=3.625 "; NEG_D=-21.75 "; NEG_F=-26.188 "; P=0.688 "; R=16.75 "; R3=-12.563 "; R4=-12.563 "; S=7.375 "; SECOND_CURVE=1.523 "; T=1.688 "; T3=4.375 "; THIRD_CURVE=2.031 "; Type Comments=Industrial Material Handler Backward Inclined Radial Blade Belt Driven Single Width Single Inlet Arrangement 1_9; U=9.813 "; UNIT_SIZE=130; W=8 "; X=18.625 "; Y=17 "; Z=24.625 "
- 150_MH_ARR_1_9: 2S=16.438 "; 2T=3.875 "; 91_AA=17.176 "; A=14.063 "; A+.25=14.313 "; A/2=7.031 "; A/5=2.813 "; AA=18.875 "; B=12.563 "; B3=12.813 "; B4=-6.406 "; B5=6.406 "; BB=18 "; C=15 "; C3=7.375 "; C4=9.5 "; D=25.25 "; D3=-25.125 "; DimQ=10.75 "; E=13 "; E_LESS_2=11 "; F=31.75 "; G=41.313 "; H=47.625 "; HALF_B=6.281 "; HALF_C=7.5 "; HALF_E=6.5 "; HALF_M=8.875 "; HALF_P=0.344 "; HALF_T=0.969 "; J=5 "; K=12.25 "; L=20.625 "; M=17.75 "; M3=14.938 "; M4=14.938 "; Model=MH; N=22.375 "; NA=8.313 "; NA3=4.156 "; NEG_D=-25.25 "; NEG_F=-31.75 "; P=0.688 "; R=21.5 "; R3=-16.125 "; R4=-16.125 "; S=8.219 "; SECOND_CURVE=1.758 "; T=1.938 "; T3=4.875 "; THIRD_CURVE=2.344 "; Type Comments=Industrial Material Handler Backward Inclined Radial Blade Belt Driven Single Width Single Inlet Arrangement 1_9; U=10.688 "; UNIT_SIZE=150; W=8 "; X=21.5 "; Y=19.75 "; Z=28.375 "
- 170_MH_ARR_1_9: 2S=18.125 "; 2T=4.375 "; 91_AA=19.338 "; A=16 "; A+.25=16.25 "; A/2=8 "; A/5=3.2 "; AA=21.25 "; B=14.25 "; B3=14.5 "; B4=-7.25 "; B5=7.25 "; BB=20.25 "; C=17 "; C3=8.375 "; C4=10.5 "; D=28.25 "; D3=-28.125 "; DimQ=10.75 "; E=13.875 "; E_LESS_2=11.875 "; F=32.563 "; G=43 "; H=53.625 "; HALF_B=7.125 "; HALF_C=8.5 "; HALF_E=6.938 "; HALF_M=10.063 "; HALF_P=0.344 "; HALF_T=1.094 "; J=6 "; K=13.125 "; L=23.75 "; M=20.125 "; M3=16.925 "; M4=16.925 "; Model=MH; N=25.375 "; NA=9.375 "; NA3=4.688 "; NEG_D=-28.25 "; NEG_F=-32.563 "; P=0.688 "; R=21.5 "; R3=-16.125 "; R4=-16.125 "; S=9.063 "; SECOND_CURVE=2 "; T=2.188 "; T3=5.375 "; THIRD_CURVE=2.667 "; Type Comments=Industrial Material Handler Backward Inclined Radial Blade Belt Driven Single Width Single Inlet Arrangement 1_9; U=11.5 "; UNIT_SIZE=170; W=8 "; X=24.563 "; Y=22.5 "; Z=32.188 "
- 190_MH_ARR_1_9: 2S=19.875 "; 2T=4.875 "; 91_AA=21.613 "; A=17.813 "; A+.25=18.063 "; A/2=8.906 "; A/5=3.563 "; AA=23.75 "; B=15.875 "; B3=16.125 "; B4=-8.063 "; B5=8.063 "; BB=22.625 "; C=19 "; C3=9.375 "; C4=11.5 "; D=31.25 "; D3=-31.125 "; DimQ=11.375 "; E=15.313 "; E_LESS_2=13.313 "; F=34.688 "; G=46 "; H=59.5 "; HALF_B=7.938 "; HALF_C=9.5 "; HALF_E=7.656 "; HALF_M=11.219 "; HALF_P=0.344 "; HALF_T=1.219 "; J=6 "; K=14.563 "; L=25.938 "; M=22.438 "; M3=18.875 "; M4=18.875 "; Model=MH; N=28.25 "; NA=10.438 "; NA3=5.219 "; NEG_D=-31.25 "; NEG_F=-34.688 "; P=0.688 "; R=22.75 "; R3=-17.063 "; R4=-17.063 "; S=9.938 "; SECOND_CURVE=2.227 "; T=2.438 "; T3=5.875 "; THIRD_CURVE=2.969 "; Type Comments=Industrial Material Handler Backward Inclined Radial Blade Belt Driven Single Width Single Inlet Arrangement 1_9; U=12.313 "; UNIT_SIZE=190; W=8 "; X=27.125 "; Y=24.875 "; Z=35.813 "
- 210_MH_ARR_1_9: 2S=21.313 "; 2T=4.875 "; 91_AA=23.433 "; A=19.75 "; A+.25=20 "; A/2=9.875 "; A/5=3.95 "; AA=25.75 "; B=17.563 "; B3=17.813 "; B4=-8.906 "; B5=8.906 "; BB=24.375 "; C=21 "; C3=10.375 "; C4=12.5 "; D=34.5 "; D3=-34.375 "; DimQ=12.75 "; E=16.563 "; E_LESS_2=14.563 "; F=38.25 "; G=50.375 "; H=65.75 "; HALF_B=8.781 "; HALF_C=10.5 "; HALF_E=8.281 "; HALF_M=11.5 "; HALF_P=0.344 "; HALF_T=1.219 "; J=6 "; K=15.813 "; L=28.5 "; M=23 "; M3=19.05 "; M4=19.05 "; Model=MH; N=31.25 "; NA=11.5 "; NA3=5.75 "; NEG_D=-34.5 "; NEG_F=-38.25 "; P=0.688 "; R=25.5 "; R3=-19.125 "; R4=-19.125 "; S=10.656 "; SECOND_CURVE=2.469 "; T=2.438 "; T3=5.875 "; THIRD_CURVE=3.292 "; Type Comments=Industrial Material Handler Backward Inclined Radial Blade Belt Driven Single Width Single Inlet Arrangement 1_9; U=13.188 "; UNIT_SIZE=210; W=8 "; X=29.875 "; Y=27.125 "; Z=38.375 "
- 230_MH_ARR_1_9: 2S=24.625 "; 2T=5.375 "; 91_AA=25.764 "; A=21.625 "; A+.25=21.875 "; A/2=10.813 "; A/5=4.325 "; AA=28.313 "; B=19.25 "; B3=19.5 "; B4=-9.75 "; B5=9.75 "; BB=26.813 "; C=23 "; C3=11.375 "; C4=13.5 "; D=37.5 "; D3=-37.375 "; DimQ=13.438 "; E=18.813 "; E_LESS_2=16.813 "; F=41.125 "; G=55.25 "; H=71.813 "; HALF_B=9.625 "; HALF_C=11.5 "; HALF_E=9.406 "; HALF_M=13 "; HALF_P=0.406 "; HALF_T=1.344 "; J=7 "; K=17.563 "; L=31.25 "; M=26 "; M3=21.675 "; M4=21.675 "; Model=MH; N=34.313 "; NA=12.688 "; NA3=6.344 "; NEG_D=-37.5 "; NEG_F=-41.125 "; P=0.813 "; R=26.875 "; R3=-20.156 "; R4=-20.156 "; S=12.313 "; SECOND_CURVE=2.703 "; T=2.688 "; T3=6.375 "; THIRD_CURVE=3.604 "; Type Comments=Industrial Material Handler Backward Inclined Radial Blade Belt Driven Single Width Single Inlet Arrangement 1_9; U=15.125 "; UNIT_SIZE=230; W=8 "; X=32.813 "; Y=29.813 "; Z=42.625 "
- 260_MH_ARR_1_9: 2S=27.125 "; 2T=5.375 "; 91_AA=29.006 "; A=24.438 "; A+.25=24.688 "; A/2=12.219 "; A/5=4.888 "; AA=31.875 "; B=21.75 "; B3=22 "; B4=-11 "; B5=11 "; BB=30.25 "; C=26 "; C3=12.875 "; C4=15 "; D=41.75 "; D3=-41.625 "; DimQ=13.875 "; E=20.625 "; E_LESS_2=18.625 "; F=43.938 "; G=58.688 "; H=82.938 "; HALF_B=10.875 "; HALF_C=13 "; HALF_E=10.313 "; HALF_M=14.5 "; HALF_P=0.406 "; HALF_T=1.344 "; J=7 "; K=19.375 "; L=35.125 "; M=29 "; M3=24.113 "; M4=24.113 "; Model=MH; N=41.188 "; NA=16.75 "; NA3=8.375 "; NEG_D=-41.75 "; NEG_F=-43.938 "; P=0.813 "; R=27.75 "; R3=-20.813 "; R4=-20.813 "; S=13.563 "; SECOND_CURVE=3.055 "; T=2.688 "; T3=6.375 "; THIRD_CURVE=4.073 "; Type Comments=Industrial Material Handler Backward Inclined Radial Blade Belt Driven Single Width Single Inlet Arrangement 1_9; U=16.375 "; UNIT_SIZE=260; W=8 "; X=38.188 "; Y=33.5 "; Z=49.625 "
- 290_MH_ARR_1_9: 2S=29.625 "; 2T=5.875 "; 91_AA=32.533 "; A=27.313 "; A+.25=27.563 "; A/2=13.656 "; A/5=5.463 "; AA=35.75 "; B=24.25 "; B3=24.5 "; B4=-12.25 "; B5=12.25 "; BB=33.875 "; C=29 "; C3=14.375 "; C4=16.5 "; D=46.5 "; D3=-46.375 "; DimQ=14.375 "; E=22.5 "; E_LESS_2=20.5 "; F=45.563 "; G=62.188 "; H=92.5 "; HALF_B=12.125 "; HALF_C=14.5 "; HALF_E=11.25 "; HALF_M=15.875 "; HALF_P=0.406 "; HALF_T=1.469 "; J=8 "; K=21.25 "; L=39.5 "; M=31.75 "; M3=26.288 "; M4=26.288 "; Model=MH; N=45.875 "; NA=18.563 "; NA3=9.281 "; NEG_D=-46.5 "; NEG_F=-45.563 "; P=0.813 "; R=28.75 "; R3=-21.563 "; R4=-21.563 "; S=14.813 "; SECOND_CURVE=3.414 "; T=2.938 "; T3=6.875 "; THIRD_CURVE=4.552 "; Type Comments=Industrial Material Handler Backward Inclined Radial Blade Belt Driven Single Width Single Inlet Arrangement 1_9; U=17.625 "; UNIT_SIZE=290; W=8 "; X=42.688 "; Y=37.625 "; Z=54.875 "
- 70_MH_ARR_1_9: 2S=8.5 "; 2T=2.375 "; 91_AA=8.019 "; A=6.625 "; A+.25=6.875 "; A/2=3.313 "; A/5=1.325 "; AA=8.813 "; B=5.875 "; B3=6.125 "; B4=-3.063 "; B5=3.063 "; BB=8.375 "; C=7 "; C3=3.375 "; C4=5.5 "; D=14.25 "; D3=-14.125 "; DimQ=7.438 "; E=9.688 "; E_LESS_2=7.688 "; F=21.063 "; G=26.25 "; H=24.188 "; HALF_B=2.938 "; HALF_C=3.5 "; HALF_E=4.844 "; HALF_M=4.156 "; HALF_P=0.281 "; HALF_T=0.594 "; J=4 "; K=9.188 "; L=9.688 "; M=8.313 "; M3=6.988 "; M4=6.988 "; Model=MH; N=10.563 "; NA=3.938 "; NA3=1.969 "; NEG_D=-14.25 "; NEG_F=-21.063 "; P=0.563 "; R=14.875 "; R3=-11.156 "; R4=-11.156 "; S=4.25 "; SECOND_CURVE=0.828 "; T=1.188 "; T3=3.375 "; THIRD_CURVE=1.104 "; Type Comments=Industrial Material Handler Backward Inclined Radial Blade Belt Driven Single Width Single Inlet Arrangement 1_9; U=6.188 "; UNIT_SIZE=70; W=6 "; X=10.125 "; Y=9.25 "; Z=13.375 "
- 90_MH_ARR_1_9: 2S=10.125 "; 2T=2.875 "; 91_AA=10.181 "; A=8.438 "; A+.25=8.688 "; A/2=4.219 "; A/5=1.688 "; AA=11.188 "; B=7.5 "; B3=7.75 "; B4=-3.875 "; B5=3.875 "; BB=10.625 "; C=9 "; C3=4.375 "; C4=6.5 "; D=15.25 "; D3=-15.125 "; DimQ=7.438 "; E=9.688 "; E_LESS_2=7.688 "; F=21.875 "; G=27.875 "; H=28.75 "; HALF_B=3.75 "; HALF_C=4.5 "; HALF_E=4.844 "; HALF_M=5.313 "; HALF_P=0.281 "; HALF_T=0.719 "; J=4 "; K=9.188 "; L=12.313 "; M=10.625 "; M3=8.938 "; M4=8.938 "; Model=MH; N=13.5 "; NA=5.063 "; NA3=2.531 "; NEG_D=-15.25 "; NEG_F=-21.875 "; P=0.563 "; R=14.875 "; R3=-11.156 "; R4=-11.156 "; S=5.063 "; SECOND_CURVE=1.055 "; T=1.438 "; T3=3.875 "; THIRD_CURVE=1.406 "; Type Comments=Industrial Material Handler Backward Inclined Radial Blade Belt Driven Single Width Single Inlet Arrangement 1_9; U=7 "; UNIT_SIZE=90; W=6 "; X=12.938 "; Y=11.75 "; Z=17.063 "

## geometry (parser evidence)
native form markers: Sweep x4
no freeform markers — native parametric forms only
